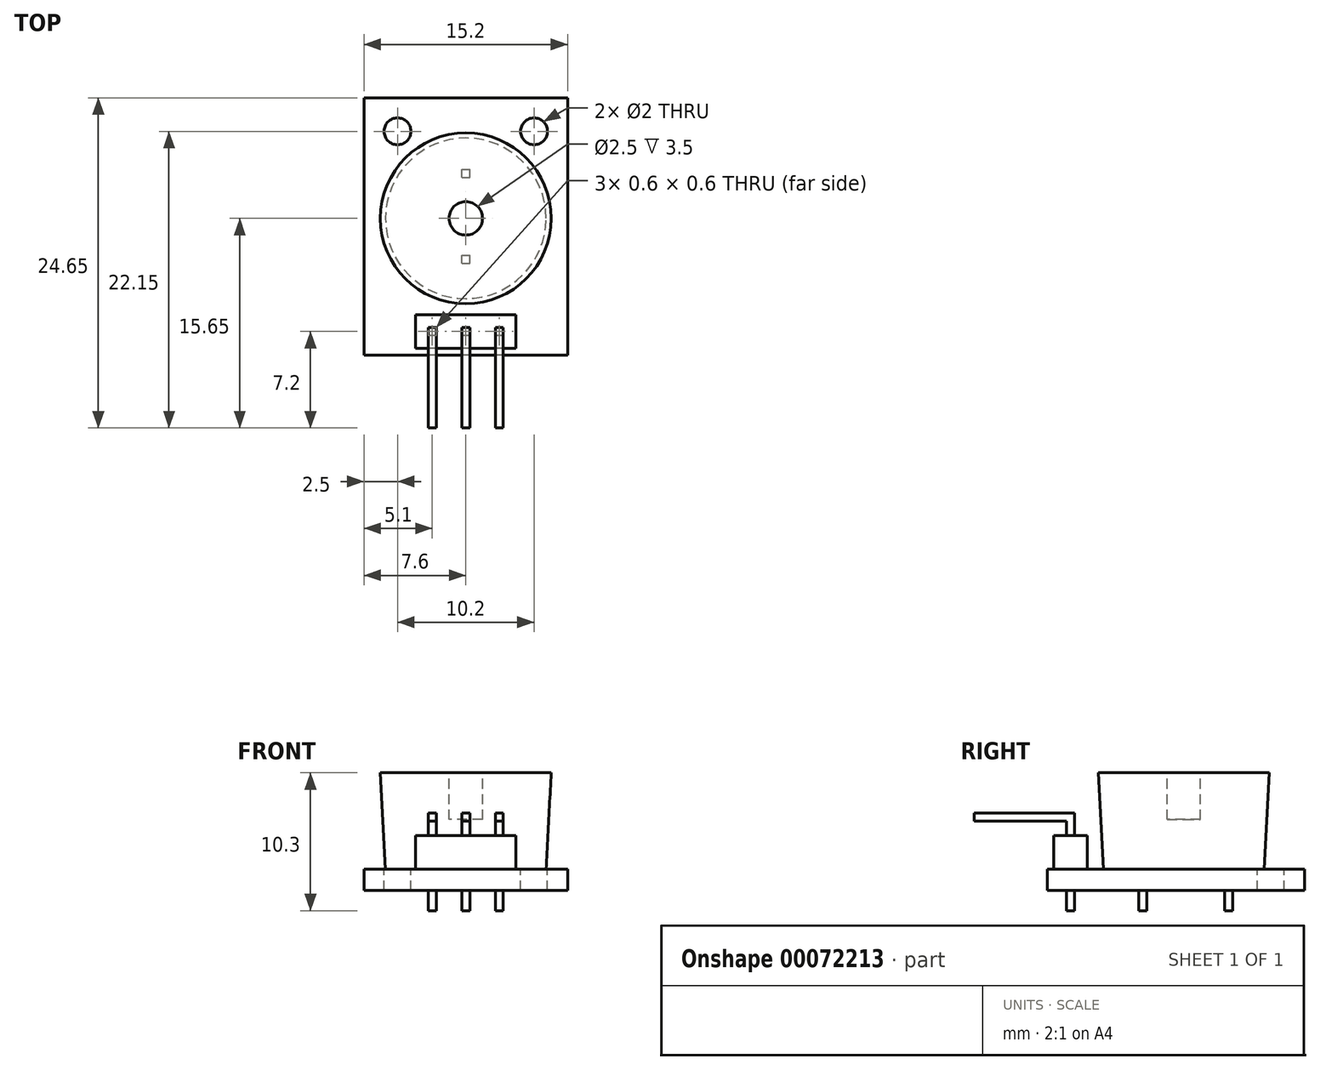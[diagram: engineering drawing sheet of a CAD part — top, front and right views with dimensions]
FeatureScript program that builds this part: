
annotation { "Feature Type Name" : "Feature", "Feature Type Description" : "" }
export const myFeature = defineFeature(function(context is Context, id is Id, definition is map)
    precondition{}
    {
        {
            var Q0;
            Q0=qCreatedBy(makeId("Top.planeOp"),FACE);
            var sketch = newSketch(context, id + "F0", { "sketchPlane" : qUnion([Q0])});
            skLineSegment(sketch, "E0.rect.bottom", {"start": v(7.6, 9.6) * mm, "end": v(-7.6, 9.6) * mm});
            skLineSegment(sketch, "E0.rect.top", {"start": v(7.6, -9.6) * mm, "end": v(-7.6, -9.6) * mm});
            skLineSegment(sketch, "E0.rect.left", {"start": v(7.6, 9.6) * mm, "end": v(7.6, -9.6) * mm});
            skLineSegment(sketch, "E0.rect.right", {"start": v(-7.6, 9.6) * mm, "end": v(-7.6, -9.6) * mm});
            skPoint(sketch, "E0.rect.middle", {"position": v(0, 0) * mm});
            skSolve(sketch);
        }
        {
            var Q0;
            Q0=qSketchRegion(id+"F0",true);
            extrude(context, id + "F1", {"entities" : qUnion([Q0]), "depth" : 1.6 * mm});
        }
        {
            var Q0;
            Q0=makeQuery(id+"F1.opExtrude","CAP_FACE",FACE,{"disambiguationData":[OSD([sQuery(id+"F0.wireOp",EDGE,"E0.rect.bottom"),sQuery(id+"F0.wireOp",EDGE,"E0.rect.top"),sQuery(id+"F0.wireOp",EDGE,"E0.rect.left"),sQuery(id+"F0.wireOp",EDGE,"E0.rect.right")])],"isStart":false});
            var sketch = newSketch(context, id + "F2", { "sketchPlane" : qUnion([Q0])});
            skCircle(sketch, "E1", {"center": v(0, 0.6) * mm, "radius": 6 * mm});
            skSolve(sketch);
        }
        {
            var Q0;
            Q0=qSketchRegion(id+"F2",true);
            extrude(context, id + "F3", {"entities" : qUnion([Q0]), "operationType" : NewBodyOperationType.ADD, "depth" : 7.2 * mm, "hasDraft" : true, "draftAngle" : 3 * degree});
        }
        {
            var Q0;
            Q0=makeQuery(id+"F3.opExtrude","CAP_FACE",FACE,{"disambiguationData":[OSD([sQuery(id+"F2.wireOp",EDGE,"E1")])],"isStart":false});
            var sketch = newSketch(context, id + "F4", { "sketchPlane" : qUnion([Q0])});
            skCircle(sketch, "E2", {"center": v(0, 0.6) * mm, "radius": 1.25 * mm});
            skSolve(sketch);
        }
        {
            var Q0;
            Q0=qSketchRegion(id+"F4",true);
            extrude(context, id + "F5", {"entities" : qUnion([Q0]), "operationType" : NewBodyOperationType.REMOVE, "oppositeDirection" : true, "depth" : 3.5 * mm});
        }
        {
            var Q0;
            Q0=makeQuery(id+"F1.opExtrude","CAP_FACE",FACE,{"disambiguationData":[OSD([sQuery(id+"F0.wireOp",EDGE,"E0.rect.bottom"),sQuery(id+"F0.wireOp",EDGE,"E0.rect.top"),sQuery(id+"F0.wireOp",EDGE,"E0.rect.left"),sQuery(id+"F0.wireOp",EDGE,"E0.rect.right")])],"isStart":false});
            var sketch = newSketch(context, id + "F6", { "sketchPlane" : qUnion([Q0])});
            skCircle(sketch, "E3", {"center": v(-5.1, 7.1) * mm, "radius": 1 * mm});
            skCircle(sketch, "E4.MirrorC", {"center": v(5.1, 7.1) * mm, "radius": 1 * mm});
            skSolve(sketch);
        }
        {
            var Q0;
            Q0=qSketchRegion(id+"F6",true);
            extrude(context, id + "F7", {"entities" : qUnion([Q0]), "operationType" : NewBodyOperationType.REMOVE, "oppositeDirection" : true, "depth" : 25 * mm});
        }
        {
            var Q0;
            Q0=makeQuery(id+"F1.opExtrude","CAP_FACE",FACE,{"disambiguationData":[OSD([sQuery(id+"F0.wireOp",EDGE,"E0.rect.bottom"),sQuery(id+"F0.wireOp",EDGE,"E0.rect.top"),sQuery(id+"F0.wireOp",EDGE,"E0.rect.left"),sQuery(id+"F0.wireOp",EDGE,"E0.rect.right")])],"isStart":false});
            var sketch = newSketch(context, id + "F8", { "sketchPlane" : qUnion([Q0])});
            skLineSegment(sketch, "E5.rect.bottom", {"start": v(3.75, -6.6) * mm, "end": v(-3.75, -6.6) * mm});
            skLineSegment(sketch, "E5.rect.top", {"start": v(3.75, -9.1) * mm, "end": v(-3.75, -9.1) * mm});
            skLineSegment(sketch, "E5.rect.left", {"start": v(3.75, -6.6) * mm, "end": v(3.75, -9.1) * mm});
            skLineSegment(sketch, "E5.rect.right", {"start": v(-3.75, -6.6) * mm, "end": v(-3.75, -9.1) * mm});
            skPoint(sketch, "E5.rect.middle", {"position": v(0, -7.85) * mm});
            skSolve(sketch);
        }
        {
            var Q0;
            Q0=qSketchRegion(id+"F8",true);
            extrude(context, id + "F9", {"entities" : qUnion([Q0]), "operationType" : NewBodyOperationType.ADD, "depth" : 2.5 * mm});
        }
        {
            var Q0;
            Q0=qCreatedBy(makeId("Top.planeOp"),FACE);
            cPlane(context, id + "F10", {"entities" : qUnion([Q0]), "cplaneType" : CPlaneType.OFFSET, "offset" : 1.5 * mm, "oppositeDirection" : true, "width" : 150 * mm, "height" : 150 * mm});
        }
        {
            var Q0;
            Q0=qCreatedBy(id+"F10.planeOp",FACE);
            var sketch = newSketch(context, id + "F11", { "sketchPlane" : qUnion([Q0])});
            skLineSegment(sketch, "E6.rect.bottom", {"start": v(-0.3, -7.55) * mm, "end": v(0.3, -7.55) * mm});
            skLineSegment(sketch, "E6.rect.top", {"start": v(-0.3, -8.15) * mm, "end": v(0.3, -8.15) * mm});
            skLineSegment(sketch, "E6.rect.left", {"start": v(-0.3, -7.55) * mm, "end": v(-0.3, -8.15) * mm});
            skLineSegment(sketch, "E6.rect.right", {"start": v(0.3, -7.55) * mm, "end": v(0.3, -8.15) * mm});
            skPoint(sketch, "E6.rect.middle", {"position": v(0, -7.85) * mm});
            skLineSegment(sketch, "E7.1.0.0", {"start": v(2.8, -7.55) * mm, "end": v(2.8, -8.15) * mm});
            skLineSegment(sketch, "E7.1.0.1", {"start": v(2.2, -8.15) * mm, "end": v(2.8, -8.15) * mm});
            skLineSegment(sketch, "E7.1.0.2", {"start": v(2.2, -7.55) * mm, "end": v(2.2, -8.15) * mm});
            skLineSegment(sketch, "E7.1.0.3", {"start": v(2.2, -7.55) * mm, "end": v(2.8, -7.55) * mm});
            skLineSegment(sketch, "E7.direction1", {"start": v(-0.3, -8.15) * mm, "end": v(2.2, -8.15) * mm, "construction": true});
            skLineSegment(sketch, "E8.MirrorCS", {"start": v(-2.2, -7.55) * mm, "end": v(-2.2, -8.15) * mm});
            skLineSegment(sketch, "E9.MirrorCS", {"start": v(-2.8, -7.55) * mm, "end": v(-2.8, -8.15) * mm});
            skLineSegment(sketch, "E10.MirrorCS", {"start": v(-2.2, -7.55) * mm, "end": v(-2.8, -7.55) * mm});
            skLineSegment(sketch, "E11.MirrorCS", {"start": v(-2.2, -8.15) * mm, "end": v(-2.8, -8.15) * mm});
            skLineSegment(sketch, "E12.rect.bottom", {"start": v(0.3, 4.25) * mm, "end": v(-0.3, 4.25) * mm});
            skLineSegment(sketch, "E12.rect.top", {"start": v(0.3, 3.65) * mm, "end": v(-0.3, 3.65) * mm});
            skLineSegment(sketch, "E12.rect.left", {"start": v(0.3, 4.25) * mm, "end": v(0.3, 3.65) * mm});
            skLineSegment(sketch, "E12.rect.right", {"start": v(-0.3, 4.25) * mm, "end": v(-0.3, 3.65) * mm});
            skPoint(sketch, "E12.rect.middle", {"position": v(0, 3.95) * mm});
            skLineSegment(sketch, "E13.rect.bottom", {"start": v(0.3, -2.15) * mm, "end": v(-0.3, -2.15) * mm});
            skLineSegment(sketch, "E13.rect.top", {"start": v(0.3, -2.75) * mm, "end": v(-0.3, -2.75) * mm});
            skLineSegment(sketch, "E13.rect.left", {"start": v(0.3, -2.15) * mm, "end": v(0.3, -2.75) * mm});
            skLineSegment(sketch, "E13.rect.right", {"start": v(-0.3, -2.15) * mm, "end": v(-0.3, -2.75) * mm});
            skPoint(sketch, "E13.rect.middle", {"position": v(0, -2.45) * mm});
            skSolve(sketch);
        }
        {
            var Q0;
            Q0=qSketchRegion(id+"F11",true);
            extrude(context, id + "F12", {"entities" : qUnion([Q0]), "operationType" : NewBodyOperationType.ADD, "depth" : 7.3 * mm});
        }
        {
            var Q0;
            {var subQ2=sQuery(id+"F11.wireOp",EDGE,"E10.MirrorCS");Q0=makeQuery(id+"F12.boolean.opBoolean","SPLIT",FACE,{"disambiguationData":[TD([makeQuery(id+"F9.opExtrude","CAP_FACE",FACE,{"disambiguationData":[OSD([sQuery(id+"F8.wireOp",EDGE,"E5.rect.bottom"),sQuery(id+"F8.wireOp",EDGE,"E5.rect.top"),sQuery(id+"F8.wireOp",EDGE,"E5.rect.left"),sQuery(id+"F8.wireOp",EDGE,"E5.rect.right")])],"isStart":false})])],"derivedFrom":makeQuery(id+"F12.opExtrude","SWEPT_FACE",FACE,{"disambiguationData":[OSD([subQ2])]})});}
            var sketch = newSketch(context, id + "F13", { "sketchPlane" : qUnion([Q0])});
            skLineSegment(sketch, "E14.bottom", {"start": v(2.8, 5.8) * mm, "end": v(2.2, 5.8) * mm});
            skLineSegment(sketch, "E14.top", {"start": v(2.8, 5.2) * mm, "end": v(2.2, 5.2) * mm});
            skLineSegment(sketch, "E14.left", {"start": v(2.8, 5.8) * mm, "end": v(2.8, 5.2) * mm});
            skLineSegment(sketch, "E14.right", {"start": v(2.2, 5.8) * mm, "end": v(2.2, 5.2) * mm});
            skLineSegment(sketch, "E15", {"start": v(0, 5.8) * mm, "end": v(0.3, 5.8) * mm});
            skLineSegment(sketch, "E16", {"start": v(0.3, 5.8) * mm, "end": v(0.3, 5.2) * mm});
            skLineSegment(sketch, "E17", {"start": v(0.3, 5.2) * mm, "end": v(0, 5.2) * mm});
            skLineSegment(sketch, "E18.MirrorCS", {"start": v(-2.8, 5.8) * mm, "end": v(-2.8, 5.2) * mm});
            skLineSegment(sketch, "E19.MirrorCS", {"start": v(-2.8, 5.2) * mm, "end": v(-2.2, 5.2) * mm});
            skLineSegment(sketch, "E20.MirrorCS", {"start": v(-2.2, 5.8) * mm, "end": v(-2.2, 5.2) * mm});
            skLineSegment(sketch, "E21.MirrorCS", {"start": v(-2.8, 5.8) * mm, "end": v(-2.2, 5.8) * mm});
            skLineSegment(sketch, "E22.MirrorCS", {"start": v(-0.3, 5.8) * mm, "end": v(-0.3, 5.2) * mm});
            skLineSegment(sketch, "E23.MirrorCS", {"start": v(-0.3, 5.2) * mm, "end": v(0, 5.2) * mm});
            skLineSegment(sketch, "E24.MirrorCS", {"start": v(0, 5.8) * mm, "end": v(-0.3, 5.8) * mm});
            skSolve(sketch);
        }
        {
            var Q0;
            Q0=qSketchRegion(id+"F13",true);
            extrude(context, id + "F14", {"entities" : qUnion([Q0]), "operationType" : NewBodyOperationType.ADD, "oppositeDirection" : true, "depth" : 7.5 * mm});
        }
    });
